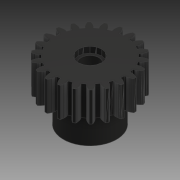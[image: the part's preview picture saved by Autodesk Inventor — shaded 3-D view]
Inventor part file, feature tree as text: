
AUTODESK INVENTOR PART (.ipt)
format: ipt  version: 2018 (Build 220112000, 112)  size: 1,167,872 bytes
history: native  units: mm
features: other x3, extrude x2, sketch x2
ambient origin geometry x8: Origin, YZ Plane, XZ Plane, XY Plane, X Axis, Y Axis, Z Axis, Center Point
bodies: Body1 (feature_tree)
feature tree (7):
  other  "ソリッド1"
  other  "openjscad"
  other  "メッシュ フィーチャ1"
  extrude  "押し出し1"  Depth=9.0mm
  extrude  "押し出し3"  Depth=4.0mm TaperAngle=0.0deg
  sketch  "スケッチ1"
  sketch  "スケッチ2"
